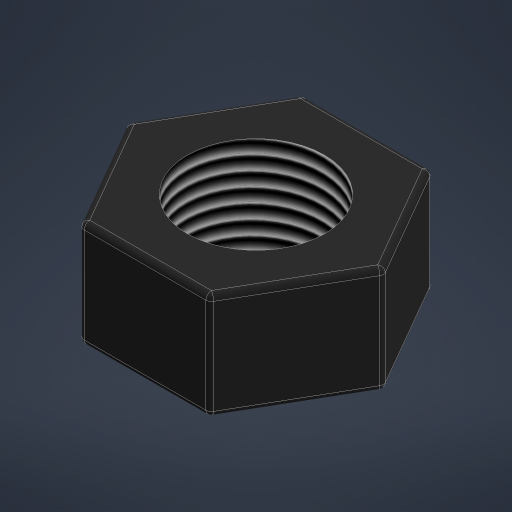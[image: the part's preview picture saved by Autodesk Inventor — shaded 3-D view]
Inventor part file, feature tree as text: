
AUTODESK INVENTOR PART (.ipt)
format: ipt  version: 2024 (Build 280153000, 153)  size: 222,208 bytes
history: native  units: mm
features: extrude x1, fillet x1, thread x1, sketch x1
ambient origin geometry x8: Origin, YZ Plane, XZ Plane, XY Plane, X Axis, Y Axis, Z Axis, Center Point
bodies: Solid1 (feature_tree)
feature tree (4):
  extrude  "Extrusion1"  Depth=3.8mm
  fillet  "Fillet1"  Radius=3.8mm
  thread  "Thread1"  [1 undecoded]
  sketch  "Sketch1"  dims[d0=7.92mm d1=4.88mm d2=3.8mm d3=0.0mm d4=0.2mm d5=3.8mm d6=0.0mm]
note: 1 required parameter value undecoded (feature->parameter linkage not recoverable at this tier; creation-order binding heuristic only, values carry confidence <= 0.55)
